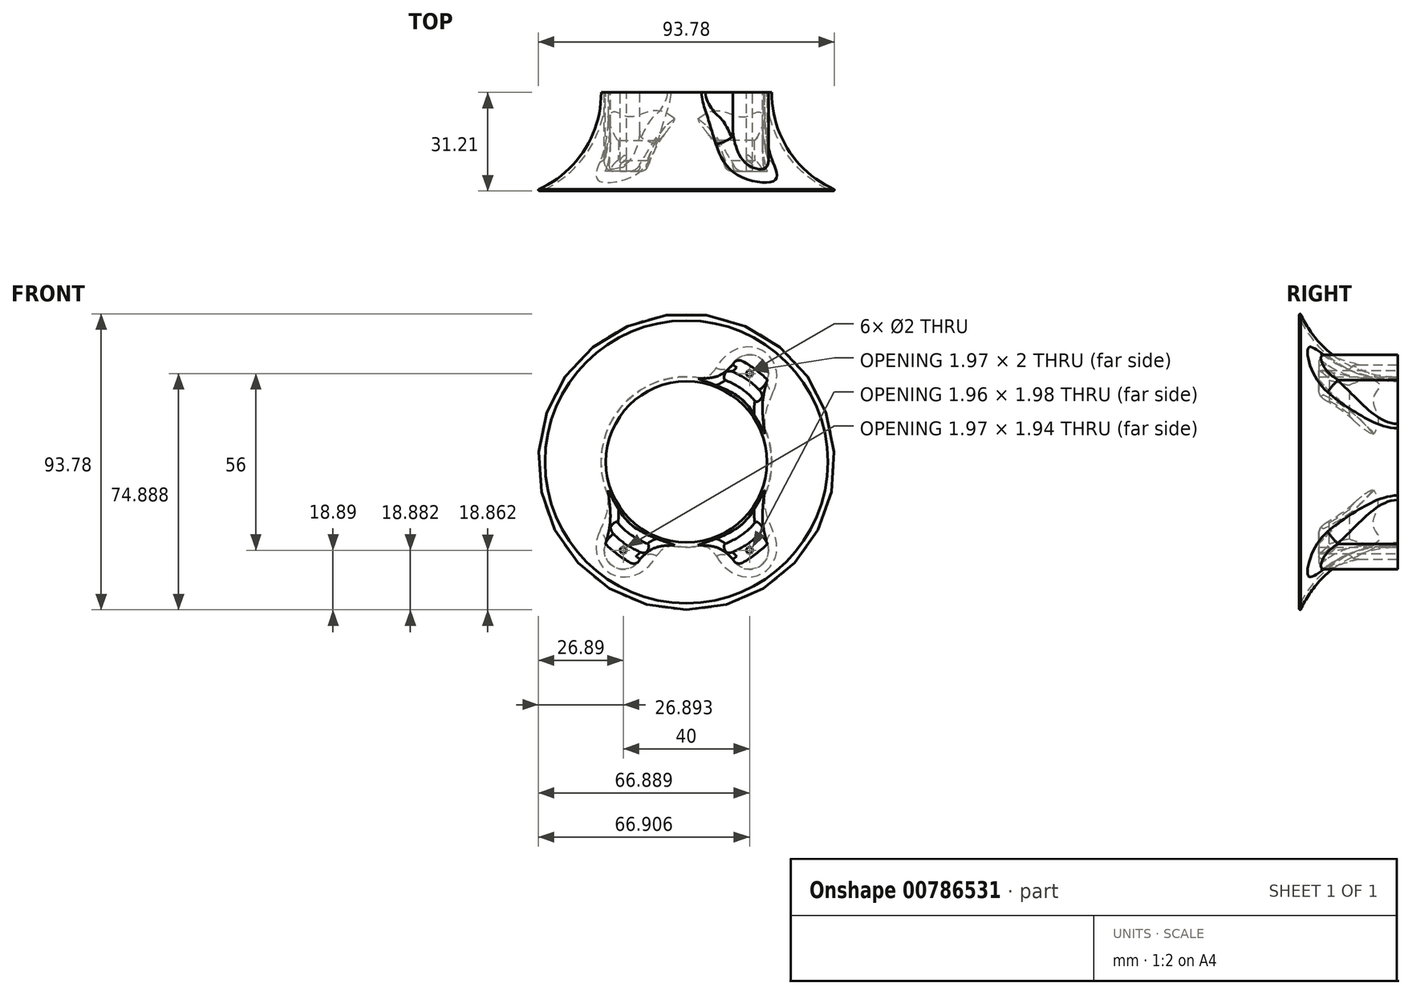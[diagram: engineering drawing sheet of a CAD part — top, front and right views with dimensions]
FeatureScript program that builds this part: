
annotation { "Feature Type Name" : "Feature", "Feature Type Description" : "" }
export const myFeature = defineFeature(function(context is Context, id is Id, definition is map)
    precondition{}
    {
        {
            var Q0;
            Q0=qCreatedBy(makeId("Top.planeOp"),FACE);
            var sketch = newSketch(context, id + "F0", { "sketchPlane" : qUnion([Q0])});
            skLineSegment(sketch, "E0", {"start": v(25.5, 0) * mm, "end": v(27, 0) * mm});
            skArc(sketch, "E1", {"start": v(27, 0) * mm, "mid": v(32.33, -18.3) * mm, "end": v(46.78, -30.7) * mm});
            skArc(sketch, "E2", {"start": v(25.5, 0) * mm, "mid": v(30.81, -18.07) * mm, "end": v(44.78, -30.7) * mm});
            skFitSpline(sketch, "E3", {"points": [v(46.78, -30.7) * mm, v(46.84, -31.06) * mm, v(46.12, -31.2) * mm, v(44.78, -30.7) * mm], "startDerivative": vector(1.91, -1.26) * mm, "endDerivative": vector(-2.92, 1.61) * mm});
            skLineSegment(sketch, "E4", {"start": v(0, -66.44) * mm, "end": v(0, 60.06) * mm, "construction": true});
            skSolve(sketch);
        }
        {
            var Q0;
            Q0=makeQuery(id+"F0.imprint","IMPRINT",FACE,{"disambiguationData":[TD([[makeQuery(id+"F0.imprint","IMPRINT",EDGE,{"derivedFrom":sQuery(id+"F0.wireOp",EDGE,"E0")}),-1.0]])]});
            var Q1;
            Q1=sQuery(id+"F0.wireOp",EDGE,"E4");
            revolve(context, id + "F1", {"surfaceOperationType" : NewSurfaceOperationType.NEW, "entities" : qUnion([Q0]), "axis" : qUnion([Q1]), "revolveType" : RevolveType.FULL});
        }
        {
            var Q0;
            Q0=qCreatedBy(makeId("Front.planeOp"),FACE);
            var sketch = newSketch(context, id + "F2", { "sketchPlane" : qUnion([Q0])});
            skArc(sketch, "E5", {"start": v(25.64, 25.96) * mm, "mid": v(22.44, 33.48) * mm, "end": v(14.7, 30.82) * mm});
            skCircle(sketch, "E6", {"center": v(20, 28) * mm, "radius": 1 * mm});
            skFitSpline(sketch, "E7", {"points": [v(14.7, 30.82) * mm, v(10.2, 27.32) * mm, v(3.6, 26.4) * mm], "startDerivative": vector(-8.6, -8.6) * mm, "endDerivative": vector(-13.55, -0.36) * mm});
            skFitSpline(sketch, "E8", {"points": [v(25.64, 25.96) * mm, v(24.12, 18.63) * mm, v(24.84, 8.96) * mm], "startDerivative": vector(-4.8, -16.33) * mm, "endDerivative": vector(2.68, -19.05) * mm});
            skFitSpline(sketch, "E9", {"points": [v(24.84, 8.96) * mm, v(18.77, 18.63) * mm, v(12.08, 23.16) * mm, v(3.6, 26.4) * mm], "startDerivative": vector(-15.4, 29.47) * mm, "endDerivative": vector(-26.8, 9.31) * mm});
            skArc(sketch, "E10.MirrorCS", {"start": v(-25.64, 25.96) * mm, "mid": v(-22.44, 33.48) * mm, "end": v(-14.7, 30.82) * mm});
            skFitSpline(sketch, "E11.MirrorCS", {"points": [v(-25.64, 25.96) * mm, v(-24.12, 18.63) * mm, v(-24.84, 8.96) * mm], "startDerivative": vector(4.8, -16.33) * mm, "endDerivative": vector(-2.68, -19.05) * mm});
            skFitSpline(sketch, "E12.MirrorCS", {"points": [v(-24.84, 8.96) * mm, v(-18.77, 18.63) * mm, v(-12.08, 23.16) * mm, v(-3.6, 26.4) * mm], "startDerivative": vector(15.4, 29.47) * mm, "endDerivative": vector(26.8, 9.31) * mm});
            skFitSpline(sketch, "E13.MirrorCS", {"points": [v(-14.7, 30.82) * mm, v(-10.2, 27.32) * mm, v(-3.6, 26.4) * mm], "startDerivative": vector(8.6, -8.6) * mm, "endDerivative": vector(13.55, -0.36) * mm});
            skFitSpline(sketch, "E14.MirrorCS", {"points": [v(25.64, -25.96) * mm, v(24.12, -18.63) * mm, v(24.84, -8.96) * mm], "startDerivative": vector(-4.8, 16.33) * mm, "endDerivative": vector(2.68, 19.05) * mm});
            skArc(sketch, "E15.MirrorCS", {"start": v(25.64, -25.96) * mm, "mid": v(22.44, -33.48) * mm, "end": v(14.7, -30.82) * mm});
            skFitSpline(sketch, "E16.MirrorCS", {"points": [v(14.7, -30.82) * mm, v(10.2, -27.32) * mm, v(3.6, -26.4) * mm], "startDerivative": vector(-8.6, 8.6) * mm, "endDerivative": vector(-13.55, 0.36) * mm});
            skFitSpline(sketch, "E17.MirrorCS", {"points": [v(24.84, -8.96) * mm, v(18.77, -18.63) * mm, v(12.08, -23.16) * mm, v(3.6, -26.4) * mm], "startDerivative": vector(-15.4, -29.47) * mm, "endDerivative": vector(-26.8, -9.31) * mm});
            skFitSpline(sketch, "E18.MirrorCS", {"points": [v(-24.84, -8.96) * mm, v(-18.77, -18.63) * mm, v(-12.08, -23.16) * mm, v(-3.6, -26.4) * mm], "startDerivative": vector(15.4, -29.47) * mm, "endDerivative": vector(26.8, -9.31) * mm});
            skFitSpline(sketch, "E19.MirrorCS", {"points": [v(-14.7, -30.82) * mm, v(-10.2, -27.32) * mm, v(-3.6, -26.4) * mm], "startDerivative": vector(8.6, 8.6) * mm, "endDerivative": vector(13.55, 0.36) * mm});
            skArc(sketch, "E20.MirrorCS", {"start": v(-25.64, -25.96) * mm, "mid": v(-22.44, -33.48) * mm, "end": v(-14.7, -30.82) * mm});
            skFitSpline(sketch, "E21.MirrorCS", {"points": [v(-25.64, -25.96) * mm, v(-24.12, -18.63) * mm, v(-24.84, -8.96) * mm], "startDerivative": vector(4.8, 16.33) * mm, "endDerivative": vector(-2.68, 19.05) * mm});
            skCircle(sketch, "E22.MirrorC", {"center": v(-20, 28) * mm, "radius": 1 * mm});
            skCircle(sketch, "E23.MirrorC", {"center": v(20, -28) * mm, "radius": 1 * mm});
            skCircle(sketch, "E24.MirrorC", {"center": v(-20, -28) * mm, "radius": 1 * mm});
            skSolve(sketch);
        }
        {
            var Q0;
            Q0=makeQuery(id+"F2.imprint","IMPRINT",FACE,{"disambiguationData":[TD([[makeQuery(id+"F2.imprint","IMPRINT",EDGE,{"derivedFrom":sQuery(id+"F2.wireOp",EDGE,"E5")}),1.0]])]});
            var Q1;
            Q1=makeQuery(id+"F2.imprint","IMPRINT",FACE,{"disambiguationData":[TD([[makeQuery(id+"F2.imprint","IMPRINT",EDGE,{"derivedFrom":sQuery(id+"F2.wireOp",EDGE,"E10.MirrorCS")}),-1.0]])]});
            var Q2;
            Q2=makeQuery(id+"F2.imprint","IMPRINT",FACE,{"disambiguationData":[TD([[makeQuery(id+"F2.imprint","IMPRINT",EDGE,{"derivedFrom":sQuery(id+"F2.wireOp",EDGE,"E18.MirrorCS")}),-1.0]])]});
            var Q3;
            Q3=makeQuery(id+"F2.imprint","IMPRINT",FACE,{"disambiguationData":[TD([[makeQuery(id+"F2.imprint","IMPRINT",EDGE,{"derivedFrom":sQuery(id+"F2.wireOp",EDGE,"E14.MirrorCS")}),1.0]])]});
            extrude(context, id + "F3", {"entities" : qUnion([Q0, Q1, Q2, Q3]), "operationType" : NewBodyOperationType.ADD, "depth" : 25 * mm, "offsetDistance" : 25 * mm});
        }
        {
            var Q0;
            Q0=makeQuery(id+"F3.opExtrude","CAP_EDGE",EDGE,{"disambiguationData":[OSD([sQuery(id+"F2.wireOp",EDGE,"E18.MirrorCS")])],"isStart":false});
            chamfer(context, id + "F4", {"entities" : qUnion([Q0]), "width" : 6 * mm});
        }
        {
            var Q0;
            {var subQ0=sQuery(id+"F2.wireOp",EDGE,"E18.MirrorCS");Q0=makeQuery(id+"F4.opChamfer","BLEND_EDGE",EDGE,{"blendedFrom":[makeQuery(id+"F3.opExtrude","CAP_EDGE",EDGE,{"disambiguationData":[OSD([subQ0])],"isStart":false}),makeQuery(id+"F3.opExtrude","SWEPT_FACE",FACE,{"disambiguationData":[OSD([subQ0])]})],"blendedInto":[makeQuery(id+"F3.opExtrude","SWEPT_FACE",FACE,{"disambiguationData":[OSD([subQ0])]})]});}
            chamfer(context, id + "F5", {"entities" : qUnion([Q0]), "width" : 9 * mm, "tangentPropagation" : true});
        }
        {
            var Q0;
            Q0=makeQuery(id+"F3.opExtrude","CAP_EDGE",EDGE,{"disambiguationData":[OSD([sQuery(id+"F2.wireOp",EDGE,"E17.MirrorCS")])],"isStart":false});
            var Q1;
            Q1=makeQuery(id+"F3.opExtrude","CAP_EDGE",EDGE,{"disambiguationData":[OSD([sQuery(id+"F2.wireOp",EDGE,"E12.MirrorCS")])],"isStart":false});
            var Q2;
            Q2=makeQuery(id+"F3.opExtrude","CAP_EDGE",EDGE,{"disambiguationData":[OSD([sQuery(id+"F2.wireOp",EDGE,"E9")])],"isStart":false});
            chamfer(context, id + "F6", {"entities" : qUnion([Q0, Q1, Q2]), "width" : 6 * mm, "tangentPropagation" : true});
        }
        {
            var Q0;
            {var subQ0=sQuery(id+"F2.wireOp",EDGE,"E9");Q0=makeQuery(id+"F6.opChamfer","BLEND_EDGE",EDGE,{"blendedFrom":[makeQuery(id+"F3.opExtrude","CAP_EDGE",EDGE,{"disambiguationData":[OSD([subQ0])],"isStart":false}),makeQuery(id+"F3.opExtrude","SWEPT_FACE",FACE,{"disambiguationData":[OSD([subQ0])]})],"blendedInto":[makeQuery(id+"F3.opExtrude","SWEPT_FACE",FACE,{"disambiguationData":[OSD([subQ0])]})]});}
            var Q1;
            {var subQ0=sQuery(id+"F2.wireOp",EDGE,"E17.MirrorCS");Q1=makeQuery(id+"F6.opChamfer","BLEND_EDGE",EDGE,{"blendedFrom":[makeQuery(id+"F3.opExtrude","CAP_EDGE",EDGE,{"disambiguationData":[OSD([subQ0])],"isStart":false}),makeQuery(id+"F3.opExtrude","SWEPT_FACE",FACE,{"disambiguationData":[OSD([subQ0])]})],"blendedInto":[makeQuery(id+"F3.opExtrude","SWEPT_FACE",FACE,{"disambiguationData":[OSD([subQ0])]})]});}
            var Q2;
            {var subQ0=sQuery(id+"F2.wireOp",EDGE,"E12.MirrorCS");Q2=makeQuery(id+"F6.opChamfer","BLEND_EDGE",EDGE,{"blendedFrom":[makeQuery(id+"F3.opExtrude","CAP_EDGE",EDGE,{"disambiguationData":[OSD([subQ0])],"isStart":false}),makeQuery(id+"F3.opExtrude","SWEPT_FACE",FACE,{"disambiguationData":[OSD([subQ0])]})],"blendedInto":[makeQuery(id+"F3.opExtrude","SWEPT_FACE",FACE,{"disambiguationData":[OSD([subQ0])]})]});}
            chamfer(context, id + "F7", {"entities" : qUnion([Q0, Q1, Q2]), "width" : 9 * mm, "tangentPropagation" : true});
        }
        {
            var Q0;
            {var subQ1=sQuery(id+"F2.wireOp",EDGE,"E9");var subQ2=sQuery(id+"F2.wireOp",EDGE,"E7");var subQ3=makeQuery(id+"F3.opExtrude","SWEPT_FACE",FACE,{"disambiguationData":[OSD([subQ1])]});Q0=makeQuery(id+"F7.opChamfer","BLEND_EDGE",EDGE,{"blendedFrom":[makeQuery(id+"F6.opChamfer","BLEND_EDGE",EDGE,{"blendedFrom":[makeQuery(id+"F3.opExtrude","CAP_EDGE",EDGE,{"disambiguationData":[OSD([subQ1])],"isStart":false}),subQ3],"blendedInto":[subQ3]}),makeQuery(id+"F3.boolean.opBoolean","SPLIT",FACE,{"disambiguationData":[TD([makeQuery(id+"F1.opRevolve","SWEPT_FACE",FACE,{"disambiguationData":[OSD([sQuery(id+"F0.wireOp",EDGE,"E2")])]})])],"derivedFrom":makeQuery(id+"F3.opExtrude","SWEPT_FACE",FACE,{"disambiguationData":[OSD([subQ2])]})})],"blendedInto":[makeQuery(id+"F3.boolean.opBoolean","SPLIT",FACE,{"disambiguationData":[TD([makeQuery(id+"F1.opRevolve","SWEPT_FACE",FACE,{"disambiguationData":[OSD([sQuery(id+"F0.wireOp",EDGE,"E2")])]})])],"derivedFrom":makeQuery(id+"F3.opExtrude","SWEPT_FACE",FACE,{"disambiguationData":[OSD([subQ2])]})})]});}
            var Q1;
            Q1=makeQuery(id+"F3.opExtrude","CAP_EDGE",EDGE,{"disambiguationData":[OSD([sQuery(id+"F2.wireOp",EDGE,"E7")])],"isStart":false});
            var Q2;
            {var subQ0=sQuery(id+"F2.wireOp",EDGE,"E7");var subQ1=sQuery(id+"F2.wireOp",EDGE,"E5");Q2=makeQuery(id+"F3.boolean.opBoolean","SPLIT",EDGE,{"disambiguationData":[TD([makeQuery(id+"F3.opExtrude","SWEPT_FACE",FACE,{"disambiguationData":[OSD([subQ0])]})])],"derivedFrom":makeQuery(id+"F3.opExtrude","CAP_EDGE",EDGE,{"disambiguationData":[OSD([subQ1])],"isStart":false})});}
            var Q3;
            {var subQ1=sQuery(id+"F2.wireOp",EDGE,"E9");var subQ2=sQuery(id+"F2.wireOp",EDGE,"E8");var subQ3=makeQuery(id+"F3.opExtrude","SWEPT_FACE",FACE,{"disambiguationData":[OSD([subQ1])]});Q3=makeQuery(id+"F7.opChamfer","BLEND_EDGE",EDGE,{"blendedFrom":[makeQuery(id+"F6.opChamfer","BLEND_EDGE",EDGE,{"blendedFrom":[makeQuery(id+"F3.opExtrude","CAP_EDGE",EDGE,{"disambiguationData":[OSD([subQ1])],"isStart":false}),subQ3],"blendedInto":[subQ3]}),makeQuery(id+"F3.boolean.opBoolean","SPLIT",FACE,{"disambiguationData":[TD([makeQuery(id+"F1.opRevolve","SWEPT_FACE",FACE,{"disambiguationData":[OSD([sQuery(id+"F0.wireOp",EDGE,"E2")])]})])],"derivedFrom":makeQuery(id+"F3.opExtrude","SWEPT_FACE",FACE,{"disambiguationData":[OSD([subQ2])]})})],"blendedInto":[makeQuery(id+"F3.boolean.opBoolean","SPLIT",FACE,{"disambiguationData":[TD([makeQuery(id+"F1.opRevolve","SWEPT_FACE",FACE,{"disambiguationData":[OSD([sQuery(id+"F0.wireOp",EDGE,"E2")])]})])],"derivedFrom":makeQuery(id+"F3.opExtrude","SWEPT_FACE",FACE,{"disambiguationData":[OSD([subQ2])]})})]});}
            var Q4;
            Q4=makeQuery(id+"F3.opExtrude","CAP_EDGE",EDGE,{"disambiguationData":[OSD([sQuery(id+"F2.wireOp",EDGE,"E8")])],"isStart":false});
            var Q5;
            {var subQ0=sQuery(id+"F2.wireOp",EDGE,"E13.MirrorCS");var subQ1=sQuery(id+"F2.wireOp",EDGE,"E12.MirrorCS");var subQ3=makeQuery(id+"F3.opExtrude","SWEPT_FACE",FACE,{"disambiguationData":[OSD([subQ1])]});Q5=makeQuery(id+"F7.opChamfer","BLEND_EDGE",EDGE,{"blendedFrom":[makeQuery(id+"F6.opChamfer","BLEND_EDGE",EDGE,{"blendedFrom":[makeQuery(id+"F3.opExtrude","CAP_EDGE",EDGE,{"disambiguationData":[OSD([subQ1])],"isStart":false}),subQ3],"blendedInto":[subQ3]}),makeQuery(id+"F3.boolean.opBoolean","SPLIT",FACE,{"disambiguationData":[TD([makeQuery(id+"F1.opRevolve","SWEPT_FACE",FACE,{"disambiguationData":[OSD([sQuery(id+"F0.wireOp",EDGE,"E2")])]})])],"derivedFrom":makeQuery(id+"F3.opExtrude","SWEPT_FACE",FACE,{"disambiguationData":[OSD([subQ0])]})})],"blendedInto":[makeQuery(id+"F3.boolean.opBoolean","SPLIT",FACE,{"disambiguationData":[TD([makeQuery(id+"F1.opRevolve","SWEPT_FACE",FACE,{"disambiguationData":[OSD([sQuery(id+"F0.wireOp",EDGE,"E2")])]})])],"derivedFrom":makeQuery(id+"F3.opExtrude","SWEPT_FACE",FACE,{"disambiguationData":[OSD([subQ0])]})})]});}
            var Q6;
            Q6=makeQuery(id+"F3.opExtrude","CAP_EDGE",EDGE,{"disambiguationData":[OSD([sQuery(id+"F2.wireOp",EDGE,"E13.MirrorCS")])],"isStart":false});
            var Q7;
            {var subQ0=sQuery(id+"F2.wireOp",EDGE,"E13.MirrorCS");var subQ1=sQuery(id+"F2.wireOp",EDGE,"E10.MirrorCS");Q7=makeQuery(id+"F3.boolean.opBoolean","SPLIT",EDGE,{"disambiguationData":[TD([makeQuery(id+"F3.opExtrude","SWEPT_FACE",FACE,{"disambiguationData":[OSD([subQ0])]})])],"derivedFrom":makeQuery(id+"F3.opExtrude","CAP_EDGE",EDGE,{"disambiguationData":[OSD([subQ1])],"isStart":false})});}
            var Q8;
            {var subQ0=sQuery(id+"F2.wireOp",EDGE,"E12.MirrorCS");var subQ1=sQuery(id+"F2.wireOp",EDGE,"E11.MirrorCS");var subQ3=makeQuery(id+"F3.opExtrude","SWEPT_FACE",FACE,{"disambiguationData":[OSD([subQ0])]});Q8=makeQuery(id+"F7.opChamfer","BLEND_EDGE",EDGE,{"blendedFrom":[makeQuery(id+"F6.opChamfer","BLEND_EDGE",EDGE,{"blendedFrom":[makeQuery(id+"F3.opExtrude","CAP_EDGE",EDGE,{"disambiguationData":[OSD([subQ0])],"isStart":false}),subQ3],"blendedInto":[subQ3]}),makeQuery(id+"F3.boolean.opBoolean","SPLIT",FACE,{"disambiguationData":[TD([makeQuery(id+"F1.opRevolve","SWEPT_FACE",FACE,{"disambiguationData":[OSD([sQuery(id+"F0.wireOp",EDGE,"E2")])]})])],"derivedFrom":makeQuery(id+"F3.opExtrude","SWEPT_FACE",FACE,{"disambiguationData":[OSD([subQ1])]})})],"blendedInto":[makeQuery(id+"F3.boolean.opBoolean","SPLIT",FACE,{"disambiguationData":[TD([makeQuery(id+"F1.opRevolve","SWEPT_FACE",FACE,{"disambiguationData":[OSD([sQuery(id+"F0.wireOp",EDGE,"E2")])]})])],"derivedFrom":makeQuery(id+"F3.opExtrude","SWEPT_FACE",FACE,{"disambiguationData":[OSD([subQ1])]})})]});}
            var Q9;
            Q9=makeQuery(id+"F3.opExtrude","CAP_EDGE",EDGE,{"disambiguationData":[OSD([sQuery(id+"F2.wireOp",EDGE,"E11.MirrorCS")])],"isStart":false});
            var Q10;
            Q10=makeQuery(id+"F3.opExtrude","CAP_EDGE",EDGE,{"disambiguationData":[OSD([sQuery(id+"F2.wireOp",EDGE,"E21.MirrorCS")])],"isStart":false});
            var Q11;
            {var subQ0=sQuery(id+"F2.wireOp",EDGE,"E20.MirrorCS");var subQ1=sQuery(id+"F2.wireOp",EDGE,"E19.MirrorCS");Q11=makeQuery(id+"F3.boolean.opBoolean","SPLIT",EDGE,{"disambiguationData":[TD([makeQuery(id+"F3.opExtrude","SWEPT_FACE",FACE,{"disambiguationData":[OSD([subQ1])]})])],"derivedFrom":makeQuery(id+"F3.opExtrude","CAP_EDGE",EDGE,{"disambiguationData":[OSD([subQ0])],"isStart":false})});}
            var Q12;
            Q12=makeQuery(id+"F3.opExtrude","CAP_EDGE",EDGE,{"disambiguationData":[OSD([sQuery(id+"F2.wireOp",EDGE,"E19.MirrorCS")])],"isStart":false});
            var Q13;
            {var subQ0=sQuery(id+"F2.wireOp",EDGE,"E18.MirrorCS");var subQ1=makeQuery(id+"F3.opExtrude","SWEPT_FACE",FACE,{"disambiguationData":[OSD([subQ0])]});var subQ3=sQuery(id+"F2.wireOp",EDGE,"E19.MirrorCS");Q13=makeQuery(id+"F5.opChamfer","BLEND_EDGE",EDGE,{"blendedFrom":[makeQuery(id+"F4.opChamfer","BLEND_EDGE",EDGE,{"blendedFrom":[makeQuery(id+"F3.opExtrude","CAP_EDGE",EDGE,{"disambiguationData":[OSD([subQ0])],"isStart":false}),subQ1],"blendedInto":[subQ1]}),makeQuery(id+"F3.boolean.opBoolean","SPLIT",FACE,{"disambiguationData":[TD([makeQuery(id+"F1.opRevolve","SWEPT_FACE",FACE,{"disambiguationData":[OSD([sQuery(id+"F0.wireOp",EDGE,"E2")])]})])],"derivedFrom":makeQuery(id+"F3.opExtrude","SWEPT_FACE",FACE,{"disambiguationData":[OSD([subQ3])]})})],"blendedInto":[makeQuery(id+"F3.boolean.opBoolean","SPLIT",FACE,{"disambiguationData":[TD([makeQuery(id+"F1.opRevolve","SWEPT_FACE",FACE,{"disambiguationData":[OSD([sQuery(id+"F0.wireOp",EDGE,"E2")])]})])],"derivedFrom":makeQuery(id+"F3.opExtrude","SWEPT_FACE",FACE,{"disambiguationData":[OSD([subQ3])]})})]});}
            var Q14;
            {var subQ0=sQuery(id+"F2.wireOp",EDGE,"E18.MirrorCS");var subQ1=makeQuery(id+"F3.opExtrude","SWEPT_FACE",FACE,{"disambiguationData":[OSD([subQ0])]});var subQ2=sQuery(id+"F2.wireOp",EDGE,"E21.MirrorCS");Q14=makeQuery(id+"F5.opChamfer","BLEND_EDGE",EDGE,{"blendedFrom":[makeQuery(id+"F4.opChamfer","BLEND_EDGE",EDGE,{"blendedFrom":[makeQuery(id+"F3.opExtrude","CAP_EDGE",EDGE,{"disambiguationData":[OSD([subQ0])],"isStart":false}),subQ1],"blendedInto":[subQ1]}),makeQuery(id+"F3.boolean.opBoolean","SPLIT",FACE,{"disambiguationData":[TD([makeQuery(id+"F1.opRevolve","SWEPT_FACE",FACE,{"disambiguationData":[OSD([sQuery(id+"F0.wireOp",EDGE,"E2")])]})])],"derivedFrom":makeQuery(id+"F3.opExtrude","SWEPT_FACE",FACE,{"disambiguationData":[OSD([subQ2])]})})],"blendedInto":[makeQuery(id+"F3.boolean.opBoolean","SPLIT",FACE,{"disambiguationData":[TD([makeQuery(id+"F1.opRevolve","SWEPT_FACE",FACE,{"disambiguationData":[OSD([sQuery(id+"F0.wireOp",EDGE,"E2")])]})])],"derivedFrom":makeQuery(id+"F3.opExtrude","SWEPT_FACE",FACE,{"disambiguationData":[OSD([subQ2])]})})]});}
            var Q15;
            {var subQ0=sQuery(id+"F2.wireOp",EDGE,"E16.MirrorCS");var subQ1=sQuery(id+"F2.wireOp",EDGE,"E15.MirrorCS");Q15=makeQuery(id+"F3.boolean.opBoolean","SPLIT",EDGE,{"disambiguationData":[TD([makeQuery(id+"F3.opExtrude","SWEPT_FACE",FACE,{"disambiguationData":[OSD([subQ0])]})])],"derivedFrom":makeQuery(id+"F3.opExtrude","CAP_EDGE",EDGE,{"disambiguationData":[OSD([subQ1])],"isStart":false})});}
            var Q16;
            Q16=makeQuery(id+"F3.opExtrude","CAP_EDGE",EDGE,{"disambiguationData":[OSD([sQuery(id+"F2.wireOp",EDGE,"E16.MirrorCS")])],"isStart":false});
            var Q17;
            {var subQ0=sQuery(id+"F2.wireOp",EDGE,"E17.MirrorCS");var subQ1=sQuery(id+"F2.wireOp",EDGE,"E16.MirrorCS");var subQ3=makeQuery(id+"F3.opExtrude","SWEPT_FACE",FACE,{"disambiguationData":[OSD([subQ0])]});Q17=makeQuery(id+"F7.opChamfer","BLEND_EDGE",EDGE,{"blendedFrom":[makeQuery(id+"F6.opChamfer","BLEND_EDGE",EDGE,{"blendedFrom":[makeQuery(id+"F3.opExtrude","CAP_EDGE",EDGE,{"disambiguationData":[OSD([subQ0])],"isStart":false}),subQ3],"blendedInto":[subQ3]}),makeQuery(id+"F3.boolean.opBoolean","SPLIT",FACE,{"disambiguationData":[TD([makeQuery(id+"F1.opRevolve","SWEPT_FACE",FACE,{"disambiguationData":[OSD([sQuery(id+"F0.wireOp",EDGE,"E2")])]})])],"derivedFrom":makeQuery(id+"F3.opExtrude","SWEPT_FACE",FACE,{"disambiguationData":[OSD([subQ1])]})})],"blendedInto":[makeQuery(id+"F3.boolean.opBoolean","SPLIT",FACE,{"disambiguationData":[TD([makeQuery(id+"F1.opRevolve","SWEPT_FACE",FACE,{"disambiguationData":[OSD([sQuery(id+"F0.wireOp",EDGE,"E2")])]})])],"derivedFrom":makeQuery(id+"F3.opExtrude","SWEPT_FACE",FACE,{"disambiguationData":[OSD([subQ1])]})})]});}
            var Q18;
            Q18=makeQuery(id+"F3.opExtrude","CAP_EDGE",EDGE,{"disambiguationData":[OSD([sQuery(id+"F2.wireOp",EDGE,"E14.MirrorCS")])],"isStart":false});
            var Q19;
            {var subQ0=sQuery(id+"F2.wireOp",EDGE,"E17.MirrorCS");var subQ2=sQuery(id+"F2.wireOp",EDGE,"E14.MirrorCS");var subQ3=makeQuery(id+"F3.opExtrude","SWEPT_FACE",FACE,{"disambiguationData":[OSD([subQ0])]});Q19=makeQuery(id+"F7.opChamfer","BLEND_EDGE",EDGE,{"blendedFrom":[makeQuery(id+"F6.opChamfer","BLEND_EDGE",EDGE,{"blendedFrom":[makeQuery(id+"F3.opExtrude","CAP_EDGE",EDGE,{"disambiguationData":[OSD([subQ0])],"isStart":false}),subQ3],"blendedInto":[subQ3]}),makeQuery(id+"F3.boolean.opBoolean","SPLIT",FACE,{"disambiguationData":[TD([makeQuery(id+"F1.opRevolve","SWEPT_FACE",FACE,{"disambiguationData":[OSD([sQuery(id+"F0.wireOp",EDGE,"E2")])]})])],"derivedFrom":makeQuery(id+"F3.opExtrude","SWEPT_FACE",FACE,{"disambiguationData":[OSD([subQ2])]})})],"blendedInto":[makeQuery(id+"F3.boolean.opBoolean","SPLIT",FACE,{"disambiguationData":[TD([makeQuery(id+"F1.opRevolve","SWEPT_FACE",FACE,{"disambiguationData":[OSD([sQuery(id+"F0.wireOp",EDGE,"E2")])]})])],"derivedFrom":makeQuery(id+"F3.opExtrude","SWEPT_FACE",FACE,{"disambiguationData":[OSD([subQ2])]})})]});}
            fillet(context, id + "F8", {"entities" : qUnion([Q0, Q1, Q2, Q3, Q4, Q5, Q6, Q7, Q8, Q9, Q10, Q11, Q12, Q13, Q14, Q15, Q16, Q17, Q18, Q19]), "radius" : 1.5 * mm, "tangentPropagation" : true, "allowEdgeOverflow" : false});
        }
        {
            var Q0;
            Q0=makeQuery(id+"F3.boolean.opBoolean","INTERSECT",EDGE,{"derivedFrom":[makeQuery(id+"F1.opRevolve","SWEPT_FACE",FACE,{"disambiguationData":[OSD([sQuery(id+"F0.wireOp",EDGE,"E1")])]}),makeQuery(id+"F3.opExtrude","SWEPT_FACE",FACE,{"disambiguationData":[OSD([sQuery(id+"F2.wireOp",EDGE,"E16.MirrorCS")])]})]});
            var Q1;
            Q1=makeQuery(id+"F3.boolean.opBoolean","INTERSECT",EDGE,{"disambiguationData":[OD(1.0)],"derivedFrom":[makeQuery(id+"F1.opRevolve","SWEPT_FACE",FACE,{"disambiguationData":[OSD([sQuery(id+"F0.wireOp",EDGE,"E1")])]}),makeQuery(id+"F3.opExtrude","SWEPT_FACE",FACE,{"disambiguationData":[OSD([sQuery(id+"F2.wireOp",EDGE,"E15.MirrorCS")])]})]});
            var Q2;
            Q2=makeQuery(id+"F3.boolean.opBoolean","INTERSECT",EDGE,{"derivedFrom":[makeQuery(id+"F1.opRevolve","SWEPT_FACE",FACE,{"disambiguationData":[OSD([sQuery(id+"F0.wireOp",EDGE,"E1")])]}),makeQuery(id+"F3.opExtrude","SWEPT_FACE",FACE,{"disambiguationData":[OSD([sQuery(id+"F2.wireOp",EDGE,"E14.MirrorCS")])]})]});
            var Q3;
            Q3=makeQuery(id+"F3.boolean.opBoolean","INTERSECT",EDGE,{"disambiguationData":[OD(0.0)],"derivedFrom":[makeQuery(id+"F1.opRevolve","SWEPT_FACE",FACE,{"disambiguationData":[OSD([sQuery(id+"F0.wireOp",EDGE,"E1")])]}),makeQuery(id+"F3.opExtrude","SWEPT_FACE",FACE,{"disambiguationData":[OSD([sQuery(id+"F2.wireOp",EDGE,"E15.MirrorCS")])]})]});
            fillet(context, id + "F9", {"entities" : qUnion([Q0, Q1, Q2, Q3]), "radius" : 5 * mm, "tangentPropagation" : true, "allowEdgeOverflow" : false});
        }
        {
            var Q0;
            Q0=makeQuery(id+"F3.boolean.opBoolean","INTERSECT",EDGE,{"derivedFrom":[makeQuery(id+"F1.opRevolve","SWEPT_FACE",FACE,{"disambiguationData":[OSD([sQuery(id+"F0.wireOp",EDGE,"E1")])]}),makeQuery(id+"F3.opExtrude","SWEPT_FACE",FACE,{"disambiguationData":[OSD([sQuery(id+"F2.wireOp",EDGE,"E19.MirrorCS")])]})]});
            var Q1;
            Q1=makeQuery(id+"F3.boolean.opBoolean","INTERSECT",EDGE,{"disambiguationData":[OD(0.0)],"derivedFrom":[makeQuery(id+"F1.opRevolve","SWEPT_FACE",FACE,{"disambiguationData":[OSD([sQuery(id+"F0.wireOp",EDGE,"E1")])]}),makeQuery(id+"F3.opExtrude","SWEPT_FACE",FACE,{"disambiguationData":[OSD([sQuery(id+"F2.wireOp",EDGE,"E20.MirrorCS")])]})]});
            var Q2;
            Q2=makeQuery(id+"F3.boolean.opBoolean","INTERSECT",EDGE,{"derivedFrom":[makeQuery(id+"F1.opRevolve","SWEPT_FACE",FACE,{"disambiguationData":[OSD([sQuery(id+"F0.wireOp",EDGE,"E1")])]}),makeQuery(id+"F3.opExtrude","SWEPT_FACE",FACE,{"disambiguationData":[OSD([sQuery(id+"F2.wireOp",EDGE,"E21.MirrorCS")])]})]});
            var Q3;
            Q3=makeQuery(id+"F3.boolean.opBoolean","INTERSECT",EDGE,{"disambiguationData":[OD(1.0)],"derivedFrom":[makeQuery(id+"F1.opRevolve","SWEPT_FACE",FACE,{"disambiguationData":[OSD([sQuery(id+"F0.wireOp",EDGE,"E1")])]}),makeQuery(id+"F3.opExtrude","SWEPT_FACE",FACE,{"disambiguationData":[OSD([sQuery(id+"F2.wireOp",EDGE,"E20.MirrorCS")])]})]});
            var Q4;
            Q4=makeQuery(id+"F3.boolean.opBoolean","INTERSECT",EDGE,{"derivedFrom":[makeQuery(id+"F1.opRevolve","SWEPT_FACE",FACE,{"disambiguationData":[OSD([sQuery(id+"F0.wireOp",EDGE,"E1")])]}),makeQuery(id+"F3.opExtrude","SWEPT_FACE",FACE,{"disambiguationData":[OSD([sQuery(id+"F2.wireOp",EDGE,"E11.MirrorCS")])]})]});
            var Q5;
            Q5=makeQuery(id+"F3.boolean.opBoolean","INTERSECT",EDGE,{"disambiguationData":[OD(0.0)],"derivedFrom":[makeQuery(id+"F1.opRevolve","SWEPT_FACE",FACE,{"disambiguationData":[OSD([sQuery(id+"F0.wireOp",EDGE,"E1")])]}),makeQuery(id+"F3.opExtrude","SWEPT_FACE",FACE,{"disambiguationData":[OSD([sQuery(id+"F2.wireOp",EDGE,"E10.MirrorCS")])]})]});
            var Q6;
            Q6=makeQuery(id+"F3.boolean.opBoolean","INTERSECT",EDGE,{"derivedFrom":[makeQuery(id+"F1.opRevolve","SWEPT_FACE",FACE,{"disambiguationData":[OSD([sQuery(id+"F0.wireOp",EDGE,"E1")])]}),makeQuery(id+"F3.opExtrude","SWEPT_FACE",FACE,{"disambiguationData":[OSD([sQuery(id+"F2.wireOp",EDGE,"E13.MirrorCS")])]})]});
            var Q7;
            Q7=makeQuery(id+"F3.boolean.opBoolean","INTERSECT",EDGE,{"disambiguationData":[OD(1.0)],"derivedFrom":[makeQuery(id+"F1.opRevolve","SWEPT_FACE",FACE,{"disambiguationData":[OSD([sQuery(id+"F0.wireOp",EDGE,"E1")])]}),makeQuery(id+"F3.opExtrude","SWEPT_FACE",FACE,{"disambiguationData":[OSD([sQuery(id+"F2.wireOp",EDGE,"E10.MirrorCS")])]})]});
            var Q8;
            Q8=makeQuery(id+"F3.boolean.opBoolean","INTERSECT",EDGE,{"derivedFrom":[makeQuery(id+"F1.opRevolve","SWEPT_FACE",FACE,{"disambiguationData":[OSD([sQuery(id+"F0.wireOp",EDGE,"E1")])]}),makeQuery(id+"F3.opExtrude","SWEPT_FACE",FACE,{"disambiguationData":[OSD([sQuery(id+"F2.wireOp",EDGE,"E7")])]})]});
            var Q9;
            Q9=makeQuery(id+"F3.boolean.opBoolean","INTERSECT",EDGE,{"disambiguationData":[OD(1.0)],"derivedFrom":[makeQuery(id+"F1.opRevolve","SWEPT_FACE",FACE,{"disambiguationData":[OSD([sQuery(id+"F0.wireOp",EDGE,"E1")])]}),makeQuery(id+"F3.opExtrude","SWEPT_FACE",FACE,{"disambiguationData":[OSD([sQuery(id+"F2.wireOp",EDGE,"E5")])]})]});
            var Q10;
            Q10=makeQuery(id+"F3.boolean.opBoolean","INTERSECT",EDGE,{"derivedFrom":[makeQuery(id+"F1.opRevolve","SWEPT_FACE",FACE,{"disambiguationData":[OSD([sQuery(id+"F0.wireOp",EDGE,"E1")])]}),makeQuery(id+"F3.opExtrude","SWEPT_FACE",FACE,{"disambiguationData":[OSD([sQuery(id+"F2.wireOp",EDGE,"E8")])]})]});
            var Q11;
            Q11=makeQuery(id+"F3.boolean.opBoolean","INTERSECT",EDGE,{"disambiguationData":[OD(0.0)],"derivedFrom":[makeQuery(id+"F1.opRevolve","SWEPT_FACE",FACE,{"disambiguationData":[OSD([sQuery(id+"F0.wireOp",EDGE,"E1")])]}),makeQuery(id+"F3.opExtrude","SWEPT_FACE",FACE,{"disambiguationData":[OSD([sQuery(id+"F2.wireOp",EDGE,"E5")])]})]});
            fillet(context, id + "F10", {"entities" : qUnion([Q0, Q1, Q2, Q3, Q4, Q5, Q6, Q7, Q8, Q9, Q10, Q11]), "radius" : 5 * mm, "tangentPropagation" : true, "allowEdgeOverflow" : false});
        }
    });
